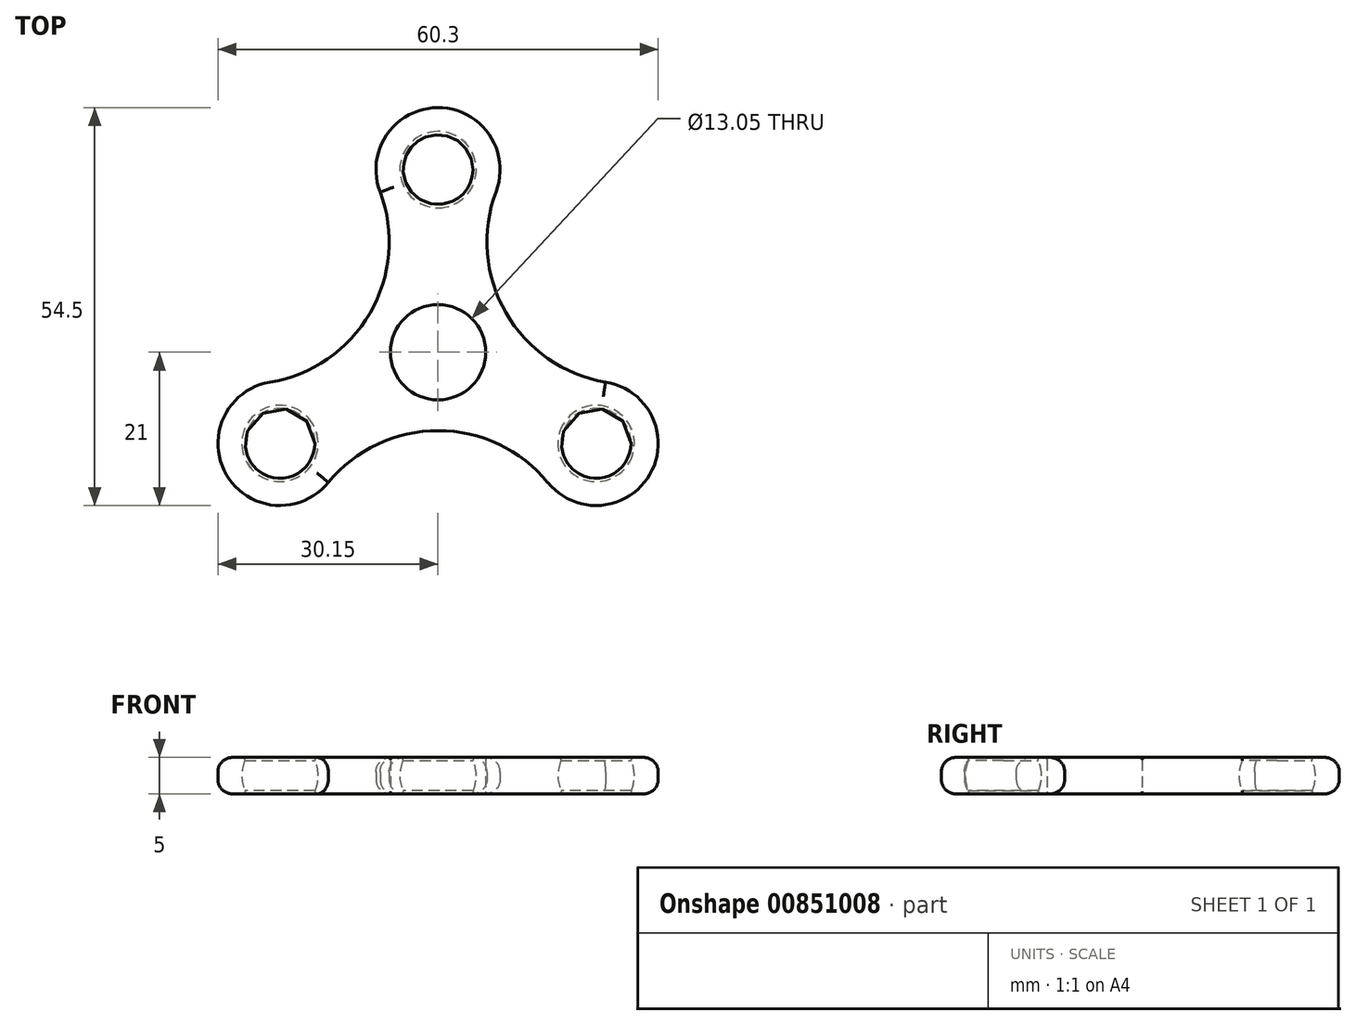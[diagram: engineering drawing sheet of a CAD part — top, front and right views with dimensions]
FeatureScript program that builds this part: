
annotation { "Feature Type Name" : "Feature", "Feature Type Description" : "" }
export const myFeature = defineFeature(function(context is Context, id is Id, definition is map)
    precondition{}
    {
        {
            var Q0;
            Q0=qCreatedBy(makeId("Top.planeOp"),FACE);
            var sketch = newSketch(context, id + "F0", { "sketchPlane" : qUnion([Q0])});
            skCircle(sketch, "E0", {"center": v(0, 0) * mm, "radius": 6.53 * mm});
            skCircle(sketch, "E1", {"center": v(0, 25) * mm, "radius": 2.5 * mm});
            skArc(sketch, "E2", {"start": v(7.95, 22) * mm, "mid": v(-0.05, 33.5) * mm, "end": v(-7.92, 21.91) * mm});
            skArc(sketch, "E3.1.0", {"start": v(-23.03, -4.11) * mm, "mid": v(-29, -16.79) * mm, "end": v(-15.02, -17.82) * mm});
            skCircle(sketch, "E3.1.1", {"center": v(-21.65, -12.5) * mm, "radius": 2.5 * mm});
            skArc(sketch, "E3.2.0", {"start": v(15.05, -17.86) * mm, "mid": v(29.02, -16.73) * mm, "end": v(22.95, -4.1) * mm});
            skCircle(sketch, "E3.2.1", {"center": v(21.65, -12.5) * mm, "radius": 2.5 * mm});
            skArc(sketch, "E4", {"start": v(-23.03, -4.11) * mm, "mid": v(-9.28, 5.41) * mm, "end": v(-7.98, 22.08) * mm});
            skArc(sketch, "E5.1.0", {"start": v(15.07, -17.89) * mm, "mid": v(-0.05, -10.75) * mm, "end": v(-15.13, -17.95) * mm});
            skArc(sketch, "E5.2.0", {"start": v(7.95, 22) * mm, "mid": v(9.33, 5.33) * mm, "end": v(23.12, -4.13) * mm});
            skLineSegment(sketch, "E6", {"start": v(0, 0) * mm, "end": v(0, 25) * mm});
            skLineSegment(sketch, "E7", {"start": v(0, 0) * mm, "end": v(-21.65, -12.5) * mm});
            skLineSegment(sketch, "E8", {"start": v(0, 0) * mm, "end": v(21.65, -12.5) * mm});
            skSolve(sketch);
        }
        {
            var Q0;
            Q0=qSketchRegion(id+"F0",true);
            extrude(context, id + "F1", {"entities" : qUnion([Q0]), "depth" : 2.5 * mm, "offsetDistance" : 25 * mm});
        }
        {
            var Q0;
            Q0=qSketchRegion(id+"F0",true);
            extrude(context, id + "F2", {"entities" : qUnion([Q0]), "operationType" : NewBodyOperationType.ADD, "oppositeDirection" : true, "depth" : 2.5 * mm, "offsetDistance" : 25 * mm});
        }
        {
            var Q0;
            Q0=qCreatedBy(makeId("Top.planeOp"),FACE);
            var sketch = newSketch(context, id + "F3", { "sketchPlane" : qUnion([Q0])});
            skLineSegment(sketch, "E9", {"start": v(0, 0) * mm, "end": v(0, 25) * mm});
            skCircle(sketch, "E10", {"center": v(0, 25) * mm, "radius": 5.23 * mm});
            skLineSegment(sketch, "E11", {"start": v(0, 30.23) * mm, "end": v(0, 25) * mm});
            skSolve(sketch);
        }
        {
            var Q0;
            {var subQ0=sQuery(id+"F3.wireOp",EDGE,"E11");Q0=makeQuery(id+"F3.imprint","IMPRINT",FACE,{"disambiguationData":[TD([[makeQuery(id+"F3.imprint","IMPRINT",EDGE,{"derivedFrom":subQ0}),1.0]])]});}
            var Q1;
            Q1=sQuery(id+"F3.wireOp",EDGE,"E11");
            revolve(context, id + "F4", {"surfaceOperationType" : NewSurfaceOperationType.NEW, "entities" : qUnion([Q0]), "axis" : qUnion([Q1]), "revolveType" : RevolveType.FULL});
        }
        {
            var Q0;
            Q0=qCreatedBy(makeId("Top.planeOp"),FACE);
            var sketch = newSketch(context, id + "F5", { "sketchPlane" : qUnion([Q0])});
            skLineSegment(sketch, "E12", {"start": v(0, 0) * mm, "end": v(0, 25) * mm});
            skLineSegment(sketch, "E13.1.0", {"start": v(0, 0) * mm, "end": v(-21.65, -12.5) * mm});
            skLineSegment(sketch, "E13.2.0", {"start": v(0, 0) * mm, "end": v(21.65, -12.5) * mm});
            skPoint(sketch, "E13.center", {"position": v(0, 0) * mm});
            skCircle(sketch, "E14", {"center": v(-21.65, -12.5) * mm, "radius": 5.23 * mm});
            skLineSegment(sketch, "E15", {"start": v(-21.65, -12.5) * mm, "end": v(-26.18, -15.11) * mm});
            skSolve(sketch);
        }
        {
            var Q0;
            {var subQ0=sQuery(id+"F5.wireOp",EDGE,"E15");Q0=makeQuery(id+"F5.imprint","IMPRINT",FACE,{"disambiguationData":[TD([[makeQuery(id+"F5.imprint","IMPRINT",EDGE,{"derivedFrom":subQ0}),-1.0]])]});}
            var Q1;
            Q1=sQuery(id+"F5.wireOp",EDGE,"E15");
            revolve(context, id + "F6", {"surfaceOperationType" : NewSurfaceOperationType.NEW, "entities" : qUnion([Q0]), "axis" : qUnion([Q1]), "revolveType" : RevolveType.FULL});
        }
        {
            var Q0;
            Q0=qCreatedBy(makeId("Top.planeOp"),FACE);
            var sketch = newSketch(context, id + "F7", { "sketchPlane" : qUnion([Q0])});
            skLineSegment(sketch, "E16", {"start": v(0, 0) * mm, "end": v(0, 25) * mm});
            skLineSegment(sketch, "E17.1.0", {"start": v(0, 0) * mm, "end": v(-21.65, -12.5) * mm});
            skLineSegment(sketch, "E17.2.0", {"start": v(0, 0) * mm, "end": v(21.65, -12.5) * mm});
            skPoint(sketch, "E17.center", {"position": v(0, 0) * mm});
            skCircle(sketch, "E18", {"center": v(21.65, -12.5) * mm, "radius": 5.23 * mm});
            skLineSegment(sketch, "E19", {"start": v(21.65, -12.5) * mm, "end": v(26.18, -15.12) * mm});
            skSolve(sketch);
        }
        {
            var Q0;
            {var subQ0=sQuery(id+"F7.wireOp",EDGE,"E19");Q0=makeQuery(id+"F7.imprint","IMPRINT",FACE,{"disambiguationData":[TD([[makeQuery(id+"F7.imprint","IMPRINT",EDGE,{"derivedFrom":subQ0}),-1.0]])]});}
            var Q1;
            Q1=sQuery(id+"F7.wireOp",EDGE,"E19");
            revolve(context, id + "F8", {"surfaceOperationType" : NewSurfaceOperationType.NEW, "entities" : qUnion([Q0]), "axis" : qUnion([Q1]), "revolveType" : RevolveType.FULL});
        }
        {
            var Q0;
            Q0=makeQuery(id+"F4.opRevolve","SWEPT_BODY",BODY,{"disambiguationData":[OSD([sQuery(id+"F3.wireOp",EDGE,"E9"),sQuery(id+"F3.wireOp",EDGE,"E10"),sQuery(id+"F3.wireOp",EDGE,"E11")])]});
            var Q1;
            Q1=makeQuery(id+"F8.opRevolve","SWEPT_BODY",BODY,{"disambiguationData":[OSD([sQuery(id+"F7.wireOp",EDGE,"E17.2.0"),sQuery(id+"F7.wireOp",EDGE,"E18"),sQuery(id+"F7.wireOp",EDGE,"E19")])]});
            var Q2;
            Q2=makeQuery(id+"F6.opRevolve","SWEPT_BODY",BODY,{"disambiguationData":[OSD([sQuery(id+"F5.wireOp",EDGE,"E13.1.0"),sQuery(id+"F5.wireOp",EDGE,"E14"),sQuery(id+"F5.wireOp",EDGE,"E15")])]});
            var Q3;
            Q3=makeQuery(id+"F1.opExtrude","SWEPT_BODY",BODY,{"disambiguationData":[OSD([sQuery(id+"F0.wireOp",EDGE,"E0"),sQuery(id+"F0.wireOp",EDGE,"E1"),sQuery(id+"F0.wireOp",EDGE,"E2"),sQuery(id+"F0.wireOp",EDGE,"E3.1.0"),sQuery(id+"F0.wireOp",EDGE,"E3.1.1"),sQuery(id+"F0.wireOp",EDGE,"E3.2.0"),sQuery(id+"F0.wireOp",EDGE,"E3.2.1"),sQuery(id+"F0.wireOp",EDGE,"E4"),sQuery(id+"F0.wireOp",EDGE,"E5.1.0"),sQuery(id+"F0.wireOp",EDGE,"E5.2.0")])]});
            booleanBodies(context, id + "F9", {"operationType" : BooleanOperationType.SUBTRACTION, "tools" : qUnion([Q0, Q1, Q2]), "targets" : qUnion([Q3])});
        }
        {
            var Q0;
            Q0=makeQuery(id+"F1.opExtrude","CAP_EDGE",EDGE,{"disambiguationData":[OSD([sQuery(id+"F0.wireOp",EDGE,"E4")])],"isStart":false});
            var Q1;
            Q1=makeQuery(id+"F1.opExtrude","CAP_EDGE",EDGE,{"disambiguationData":[OSD([sQuery(id+"F0.wireOp",EDGE,"E2")])],"isStart":false});
            var Q2;
            {var subQ0=sQuery(id+"F0.wireOp",EDGE,"E5.2.0");Q2=makeQuery(id+"F1.opExtrude","CAP_EDGE",EDGE,{"disambiguationData":[OSD([subQ0]),TDD([makeQuery(id+"F0.imprint","IMPRINT",EDGE,{"disambiguationData":[TD([[makeQuery(id+"F0.imprint","INTERSECT",VERTEX,{"derivedFrom":[sQuery(id+"F0.wireOp",EDGE,"E2"),subQ0]}),-1.0]])],"derivedFrom":subQ0})])],"isStart":false});}
            var Q3;
            {var subQ0=sQuery(id+"F0.wireOp",EDGE,"E3.1.0");Q3=makeQuery(id+"F1.opExtrude","CAP_EDGE",EDGE,{"disambiguationData":[OSD([subQ0]),TDD([makeQuery(id+"F0.imprint","IMPRINT",EDGE,{"disambiguationData":[TD([[makeQuery(id+"F0.imprint","INTERSECT",VERTEX,{"derivedFrom":[subQ0,sQuery(id+"F0.wireOp",EDGE,"E4")]}),-1.0]])],"derivedFrom":subQ0})])],"isStart":false});}
            var Q4;
            {var subQ0=sQuery(id+"F0.wireOp",EDGE,"E5.1.0");Q4=makeQuery(id+"F1.opExtrude","CAP_EDGE",EDGE,{"disambiguationData":[OSD([subQ0]),TDD([makeQuery(id+"F0.imprint","IMPRINT",EDGE,{"disambiguationData":[TD([[makeQuery(id+"F0.imprint","INTERSECT",VERTEX,{"disambiguationData":[OD(0.0)],"derivedFrom":[sQuery(id+"F0.wireOp",EDGE,"E3.1.0"),subQ0]}),1.0]])],"derivedFrom":subQ0})])],"isStart":false});}
            var Q5;
            {var subQ0=sQuery(id+"F0.wireOp",EDGE,"E3.2.0");Q5=makeQuery(id+"F1.opExtrude","CAP_EDGE",EDGE,{"disambiguationData":[OSD([subQ0]),TDD([makeQuery(id+"F0.imprint","IMPRINT",EDGE,{"disambiguationData":[TD([[makeQuery(id+"F0.imprint","INTERSECT",VERTEX,{"derivedFrom":[subQ0,sQuery(id+"F0.wireOp",EDGE,"E5.1.0")]}),-1.0]])],"derivedFrom":subQ0})])],"isStart":false});}
            var Q6;
            {var subQ0=sQuery(id+"F0.wireOp",EDGE,"E5.2.0");var subQ1=sQuery(id+"F0.wireOp",EDGE,"E3.2.0");Q6=makeQuery(id+"F1.opExtrude","CAP_EDGE",EDGE,{"disambiguationData":[OSD([subQ1]),TDD([makeQuery(id+"F0.imprint","IMPRINT",EDGE,{"disambiguationData":[TD([[makeQuery(id+"F0.imprint","INTERSECT",VERTEX,{"disambiguationData":[OD(0.0)],"derivedFrom":[subQ1,subQ0]}),1.0]])],"derivedFrom":subQ1})])],"isStart":false});}
            var Q7;
            {var subQ0=sQuery(id+"F0.wireOp",EDGE,"E5.2.0");var subQ1=sQuery(id+"F0.wireOp",EDGE,"E3.2.0");Q7=makeQuery(id+"F1.opExtrude","CAP_EDGE",EDGE,{"disambiguationData":[OSD([subQ0]),TDD([makeQuery(id+"F0.imprint","IMPRINT",EDGE,{"disambiguationData":[TD([[makeQuery(id+"F0.imprint","INTERSECT",VERTEX,{"disambiguationData":[OD(1.0)],"derivedFrom":[subQ1,subQ0]}),1.0]])],"derivedFrom":subQ0})])],"isStart":false});}
            var Q8;
            {var subQ0=sQuery(id+"F0.wireOp",EDGE,"E5.1.0");var subQ1=sQuery(id+"F0.wireOp",EDGE,"E3.1.0");Q8=makeQuery(id+"F1.opExtrude","CAP_EDGE",EDGE,{"disambiguationData":[OSD([subQ1]),TDD([makeQuery(id+"F0.imprint","IMPRINT",EDGE,{"disambiguationData":[TD([[makeQuery(id+"F0.imprint","INTERSECT",VERTEX,{"disambiguationData":[OD(0.0)],"derivedFrom":[subQ1,subQ0]}),1.0]])],"derivedFrom":subQ1})])],"isStart":false});}
            var Q9;
            {var subQ0=sQuery(id+"F0.wireOp",EDGE,"E5.1.0");var subQ1=sQuery(id+"F0.wireOp",EDGE,"E3.1.0");Q9=makeQuery(id+"F1.opExtrude","CAP_EDGE",EDGE,{"disambiguationData":[OSD([subQ0]),TDD([makeQuery(id+"F0.imprint","IMPRINT",EDGE,{"disambiguationData":[TD([[makeQuery(id+"F0.imprint","INTERSECT",VERTEX,{"disambiguationData":[OD(1.0)],"derivedFrom":[subQ1,subQ0]}),1.0]])],"derivedFrom":subQ0})])],"isStart":false});}
            var Q10;
            {var subQ0=sQuery(id+"F0.wireOp",EDGE,"E5.1.0");Q10=makeQuery(id+"F2.opExtrude","CAP_EDGE",EDGE,{"disambiguationData":[OSD([subQ0]),TDD([makeQuery(id+"F0.imprint","IMPRINT",EDGE,{"disambiguationData":[TD([[makeQuery(id+"F0.imprint","INTERSECT",VERTEX,{"disambiguationData":[OD(0.0)],"derivedFrom":[sQuery(id+"F0.wireOp",EDGE,"E3.1.0"),subQ0]}),1.0]])],"derivedFrom":subQ0})])],"isStart":false});}
            var Q11;
            {var subQ0=sQuery(id+"F0.wireOp",EDGE,"E3.1.0");Q11=makeQuery(id+"F2.opExtrude","CAP_EDGE",EDGE,{"disambiguationData":[OSD([subQ0]),TDD([makeQuery(id+"F0.imprint","IMPRINT",EDGE,{"disambiguationData":[TD([[makeQuery(id+"F0.imprint","INTERSECT",VERTEX,{"derivedFrom":[subQ0,sQuery(id+"F0.wireOp",EDGE,"E4")]}),-1.0]])],"derivedFrom":subQ0})])],"isStart":false});}
            var Q12;
            Q12=makeQuery(id+"F2.opExtrude","CAP_EDGE",EDGE,{"disambiguationData":[OSD([sQuery(id+"F0.wireOp",EDGE,"E4")])],"isStart":false});
            var Q13;
            {var subQ0=sQuery(id+"F0.wireOp",EDGE,"E5.1.0");var subQ1=sQuery(id+"F0.wireOp",EDGE,"E3.1.0");Q13=makeQuery(id+"F2.opExtrude","CAP_EDGE",EDGE,{"disambiguationData":[OSD([subQ0]),TDD([makeQuery(id+"F0.imprint","IMPRINT",EDGE,{"disambiguationData":[TD([[makeQuery(id+"F0.imprint","INTERSECT",VERTEX,{"disambiguationData":[OD(1.0)],"derivedFrom":[subQ1,subQ0]}),1.0]])],"derivedFrom":subQ0})])],"isStart":false});}
            var Q14;
            {var subQ0=sQuery(id+"F0.wireOp",EDGE,"E5.1.0");var subQ1=sQuery(id+"F0.wireOp",EDGE,"E3.1.0");Q14=makeQuery(id+"F2.opExtrude","CAP_EDGE",EDGE,{"disambiguationData":[OSD([subQ1]),TDD([makeQuery(id+"F0.imprint","IMPRINT",EDGE,{"disambiguationData":[TD([[makeQuery(id+"F0.imprint","INTERSECT",VERTEX,{"disambiguationData":[OD(0.0)],"derivedFrom":[subQ1,subQ0]}),1.0]])],"derivedFrom":subQ1})])],"isStart":false});}
            var Q15;
            {var subQ0=sQuery(id+"F0.wireOp",EDGE,"E3.2.0");Q15=makeQuery(id+"F2.opExtrude","CAP_EDGE",EDGE,{"disambiguationData":[OSD([subQ0]),TDD([makeQuery(id+"F0.imprint","IMPRINT",EDGE,{"disambiguationData":[TD([[makeQuery(id+"F0.imprint","INTERSECT",VERTEX,{"derivedFrom":[subQ0,sQuery(id+"F0.wireOp",EDGE,"E5.1.0")]}),-1.0]])],"derivedFrom":subQ0})])],"isStart":false});}
            var Q16;
            Q16=makeQuery(id+"F2.opExtrude","CAP_EDGE",EDGE,{"disambiguationData":[OSD([sQuery(id+"F0.wireOp",EDGE,"E2")])],"isStart":false});
            var Q17;
            {var subQ0=sQuery(id+"F0.wireOp",EDGE,"E5.2.0");Q17=makeQuery(id+"F2.opExtrude","CAP_EDGE",EDGE,{"disambiguationData":[OSD([subQ0]),TDD([makeQuery(id+"F0.imprint","IMPRINT",EDGE,{"disambiguationData":[TD([[makeQuery(id+"F0.imprint","INTERSECT",VERTEX,{"derivedFrom":[sQuery(id+"F0.wireOp",EDGE,"E2"),subQ0]}),-1.0]])],"derivedFrom":subQ0})])],"isStart":false});}
            var Q18;
            {var subQ0=sQuery(id+"F0.wireOp",EDGE,"E5.2.0");var subQ1=sQuery(id+"F0.wireOp",EDGE,"E3.2.0");Q18=makeQuery(id+"F2.opExtrude","CAP_EDGE",EDGE,{"disambiguationData":[OSD([subQ1]),TDD([makeQuery(id+"F0.imprint","IMPRINT",EDGE,{"disambiguationData":[TD([[makeQuery(id+"F0.imprint","INTERSECT",VERTEX,{"disambiguationData":[OD(0.0)],"derivedFrom":[subQ1,subQ0]}),1.0]])],"derivedFrom":subQ1})])],"isStart":false});}
            var Q19;
            {var subQ0=sQuery(id+"F0.wireOp",EDGE,"E5.2.0");var subQ1=sQuery(id+"F0.wireOp",EDGE,"E3.2.0");Q19=makeQuery(id+"F2.opExtrude","CAP_EDGE",EDGE,{"disambiguationData":[OSD([subQ0]),TDD([makeQuery(id+"F0.imprint","IMPRINT",EDGE,{"disambiguationData":[TD([[makeQuery(id+"F0.imprint","INTERSECT",VERTEX,{"disambiguationData":[OD(1.0)],"derivedFrom":[subQ1,subQ0]}),1.0]])],"derivedFrom":subQ0})])],"isStart":false});}
            fillet(context, id + "F10", {"entities" : qUnion([Q0, Q1, Q2, Q3, Q4, Q5, Q6, Q7, Q8, Q9, Q10, Q11, Q12, Q13, Q14, Q15, Q16, Q17, Q18, Q19]), "radius" : 2 * mm, "tangentPropagation" : true, "allowEdgeOverflow" : false});
        }
        {
            var Q0;
            Q0=makeQuery(id+"F9.opBoolean","COPY",FACE,{"derivedFrom":makeQuery(id+"F6.opRevolve","SWEPT_FACE",FACE,{"disambiguationData":[OSD([sQuery(id+"F5.wireOp",EDGE,"E14")])]})});
            var Q1;
            Q1=makeQuery(id+"F9.opBoolean","COPY",FACE,{"derivedFrom":makeQuery(id+"F8.opRevolve","SWEPT_FACE",FACE,{"disambiguationData":[OSD([sQuery(id+"F7.wireOp",EDGE,"E18")])]})});
            var Q2;
            {var subQ0=sQuery(id+"F0.wireOp",EDGE,"E0");Q2=makeQuery(id+"F2.boolean.opBoolean","MERGE",FACE,{"derivedFrom":[makeQuery(id+"F1.opExtrude","SWEPT_FACE",FACE,{"disambiguationData":[OSD([subQ0])]}),makeQuery(id+"F2.opExtrude","SWEPT_FACE",FACE,{"disambiguationData":[OSD([subQ0])]})]});}
            var Q3;
            Q3=makeQuery(id+"F9.opBoolean","COPY",FACE,{"derivedFrom":makeQuery(id+"F4.opRevolve","SWEPT_FACE",FACE,{"disambiguationData":[OSD([sQuery(id+"F3.wireOp",EDGE,"E10")])]})});
            fillet(context, id + "F11", {"entities" : qUnion([Q0, Q1, Q2, Q3]), "radius" : .3 * mm, "tangentPropagation" : true, "allowEdgeOverflow" : false});
        }
    });
